annotation { "Feature Type Name" : "Feature", "Feature Type Description" : "" }
export const myFeature = defineFeature(function(context is Context, id is Id, definition is map)
    precondition{}
    {
        {
            var Q0;
            Q0=qCreatedBy(makeId("Front.planeOp"),FACE);
            var sketch = newSketch(context, id + "F0", { "sketchPlane" : qUnion([Q0])});
            skLineSegment(sketch, "E0", {"start": v(-98.06, 0) * mm, "end": v(98.8, 0) * mm});
            skLineSegment(sketch, "E1", {"start": v(98.8, 0) * mm, "end": v(103.27, 25.4) * mm});
            skLineSegment(sketch, "E2", {"start": v(103.27, 25.4) * mm, "end": v(-102.54, 25.4) * mm});
            skLineSegment(sketch, "E3", {"start": v(-102.54, 25.4) * mm, "end": v(-98.06, 0) * mm});
            skPoint(sketch, "E4.startSnap0", {"position": v(0.37, 25.4) * mm});
            skPoint(sketch, "E4.endSnap0", {"position": v(0.37, 25.4) * mm});
            skSolve(sketch);
        }
        {
            var Q0;
            Q0=makeQuery(id+"F0.imprint","IMPRINT",FACE,{"disambiguationData":[TD([[makeQuery(id+"F0.imprint","IMPRINT",EDGE,{"derivedFrom":sQuery(id+"F0.wireOp",EDGE,"E0")}),1.0]])]});
            extrude(context, id + "F1", {"entities" : qUnion([Q0]), "depth" : 3 * mm});
        }
        {
            var Q0;
            Q0=qCreatedBy(makeId("Front.planeOp"),FACE);
            var sketch = newSketch(context, id + "F2", { "sketchPlane" : qUnion([Q0])});
            skLineSegment(sketch, "E5", {"start": v(-8.9, 25.4) * mm, "end": v(-12.03, 43.18) * mm});
            skLineSegment(sketch, "E6", {"start": v(-12.03, 43.18) * mm, "end": v(12.03, 43.18) * mm});
            skLineSegment(sketch, "E7", {"start": v(12.03, 43.18) * mm, "end": v(8.89, 25.4) * mm});
            skLineSegment(sketch, "E8", {"start": v(8.89, 25.4) * mm, "end": v(-8.9, 25.4) * mm});
            skSolve(sketch);
        }
        {
            var Q0;
            Q0=makeQuery(id+"F2.imprint","IMPRINT",FACE,{"disambiguationData":[TD([[makeQuery(id+"F2.imprint","IMPRINT",EDGE,{"derivedFrom":sQuery(id+"F2.wireOp",EDGE,"E5")}),-1.0]])]});
            extrude(context, id + "F3", {"entities" : qUnion([Q0]), "operationType" : NewBodyOperationType.ADD, "depth" : 5 * mm});
        }
        {
            var Q0;
            Q0=qCreatedBy(makeId("Front.planeOp"),FACE);
            var sketch = newSketch(context, id + "F4", { "sketchPlane" : qUnion([Q0])});
            skLineSegment(sketch, "E9", {"start": v(-11, 40.64) * mm, "end": v(-17.35, 40.64) * mm});
            skLineSegment(sketch, "E10", {"start": v(-17.35, 40.64) * mm, "end": v(-14.67, 25.4) * mm});
            skLineSegment(sketch, "E11", {"start": v(-14.67, 25.4) * mm, "end": v(-8.32, 25.4) * mm});
            skLineSegment(sketch, "E12", {"start": v(-8.32, 25.4) * mm, "end": v(-11, 40.64) * mm});
            skLineSegment(sketch, "E13.MirrorCS", {"start": v(8.32, 25.4) * mm, "end": v(11, 40.64) * mm});
            skLineSegment(sketch, "E14.MirrorCS", {"start": v(11, 40.64) * mm, "end": v(17.35, 40.64) * mm});
            skLineSegment(sketch, "E15.MirrorCS", {"start": v(17.35, 40.64) * mm, "end": v(14.67, 25.4) * mm});
            skLineSegment(sketch, "E16.MirrorCS", {"start": v(14.67, 25.4) * mm, "end": v(8.32, 25.4) * mm});
            skSolve(sketch);
        }
        {
            var Q0;
            Q0=makeQuery(id+"F4.imprint","IMPRINT",FACE,{"disambiguationData":[TD([[makeQuery(id+"F4.imprint","IMPRINT",EDGE,{"derivedFrom":sQuery(id+"F4.wireOp",EDGE,"E9")}),1.0]])]});
            var Q1;
            Q1=makeQuery(id+"F4.imprint","IMPRINT",FACE,{"disambiguationData":[TD([[makeQuery(id+"F4.imprint","IMPRINT",EDGE,{"derivedFrom":sQuery(id+"F4.wireOp",EDGE,"E13.MirrorCS")}),-1.0]])]});
            extrude(context, id + "F5", {"entities" : qUnion([Q0, Q1]), "operationType" : NewBodyOperationType.ADD, "depth" : 4 * mm});
        }
        {
            var Q0;
            Q0=qCreatedBy(makeId("Front.planeOp"),FACE);
            var sketch = newSketch(context, id + "F6", { "sketchPlane" : qUnion([Q0])});
            skLineSegment(sketch, "E17", {"start": v(-16.74, 36.07) * mm, "end": v(-23.85, 36.07) * mm});
            skLineSegment(sketch, "E18", {"start": v(-23.85, 36.07) * mm, "end": v(-19.97, 25.4) * mm});
            skLineSegment(sketch, "E19", {"start": v(-19.97, 25.4) * mm, "end": v(-14.53, 25.4) * mm});
            skLineSegment(sketch, "E20", {"start": v(-14.53, 25.4) * mm, "end": v(-16.74, 36.07) * mm});
            skLineSegment(sketch, "E21.MirrorCS", {"start": v(14.53, 25.4) * mm, "end": v(16.74, 36.07) * mm});
            skLineSegment(sketch, "E22.MirrorCS", {"start": v(16.74, 36.07) * mm, "end": v(23.85, 36.07) * mm});
            skLineSegment(sketch, "E23.MirrorCS", {"start": v(23.85, 36.07) * mm, "end": v(19.97, 25.4) * mm});
            skLineSegment(sketch, "E24.MirrorCS", {"start": v(19.97, 25.4) * mm, "end": v(14.53, 25.4) * mm});
            skSolve(sketch);
        }
        {
            var Q0;
            Q0=makeQuery(id+"F6.imprint","IMPRINT",FACE,{"disambiguationData":[TD([[makeQuery(id+"F6.imprint","IMPRINT",EDGE,{"derivedFrom":sQuery(id+"F6.wireOp",EDGE,"E17")}),1.0]])]});
            var Q1;
            Q1=makeQuery(id+"F6.imprint","IMPRINT",FACE,{"disambiguationData":[TD([[makeQuery(id+"F6.imprint","IMPRINT",EDGE,{"derivedFrom":sQuery(id+"F6.wireOp",EDGE,"E21.MirrorCS")}),-1.0]])]});
            extrude(context, id + "F7", {"entities" : qUnion([Q0, Q1]), "operationType" : NewBodyOperationType.ADD, "depth" : 2 * mm});
        }
        {
            var Q0;
            Q0=makeQuery(id+"F1.opExtrude","CAP_FACE",FACE,{"disambiguationData":[OSD([sQuery(id+"F0.wireOp",EDGE,"E0"),sQuery(id+"F0.wireOp",EDGE,"E1"),sQuery(id+"F0.wireOp",EDGE,"E2"),sQuery(id+"F0.wireOp",EDGE,"E3")])],"isStart":false});
            var sketch = newSketch(context, id + "F8", { "sketchPlane" : qUnion([Q0])});
            skLineSegment(sketch, "E25.0", {"start": v(-14.67, 23.88) * mm, "end": v(-100.72, 23.88) * mm});
            skLineSegment(sketch, "E25.1", {"start": v(-96.78, 1.52) * mm, "end": v(97.51, 1.52) * mm});
            skLineSegment(sketch, "E25.2", {"start": v(97.51, 1.52) * mm, "end": v(101.45, 23.88) * mm});
            skLineSegment(sketch, "E25.3", {"start": v(-100.72, 23.88) * mm, "end": v(-96.78, 1.52) * mm});
            skLineSegment(sketch, "E25.4", {"start": v(101.45, 23.88) * mm, "end": v(14.67, 23.88) * mm});
            skLineSegment(sketch, "E25.5", {"start": v(14.67, 23.88) * mm, "end": v(-14.67, 23.88) * mm});
            skSolve(sketch);
        }
        {
            var Q0;
            Q0=makeQuery(id+"F8.imprint","IMPRINT",FACE,{"disambiguationData":[TD([[makeQuery(id+"F8.imprint","IMPRINT",EDGE,{"derivedFrom":sQuery(id+"F8.wireOp",EDGE,"E25.0")}),-1.0]])]});
            extrude(context, id + "F9", {"entities" : qUnion([Q0]), "operationType" : NewBodyOperationType.ADD, "depth" : 1 * mm});
        }
        {
            var Q0;
            Q0=makeQuery(id+"F1.opExtrude","CAP_FACE",FACE,{"disambiguationData":[OSD([sQuery(id+"F0.wireOp",EDGE,"E0"),sQuery(id+"F0.wireOp",EDGE,"E1"),sQuery(id+"F0.wireOp",EDGE,"E2"),sQuery(id+"F0.wireOp",EDGE,"E3")])],"isStart":false});
            var sketch = newSketch(context, id + "F10", { "sketchPlane" : qUnion([Q0])});
            skText(sketch, "E26", { "text": "Pradeep Johns", "fontName": "RobotoSlab-Bold.ttf"});
            const initialGuessF10  = {"E26": [-0.07563, 0.00568, 1, 0, 0.01577]};
            skSetInitialGuess(sketch, initialGuessF10);
            skSolve(sketch);
        }
        {
            var Q0;
            Q0 = qSketchRegion(id + "F10", true);
            extrude(context, id + "F11", {"entities" : qUnion([Q0]), "operationType" : NewBodyOperationType.ADD, "depth" : 2 * mm});
        }
    });